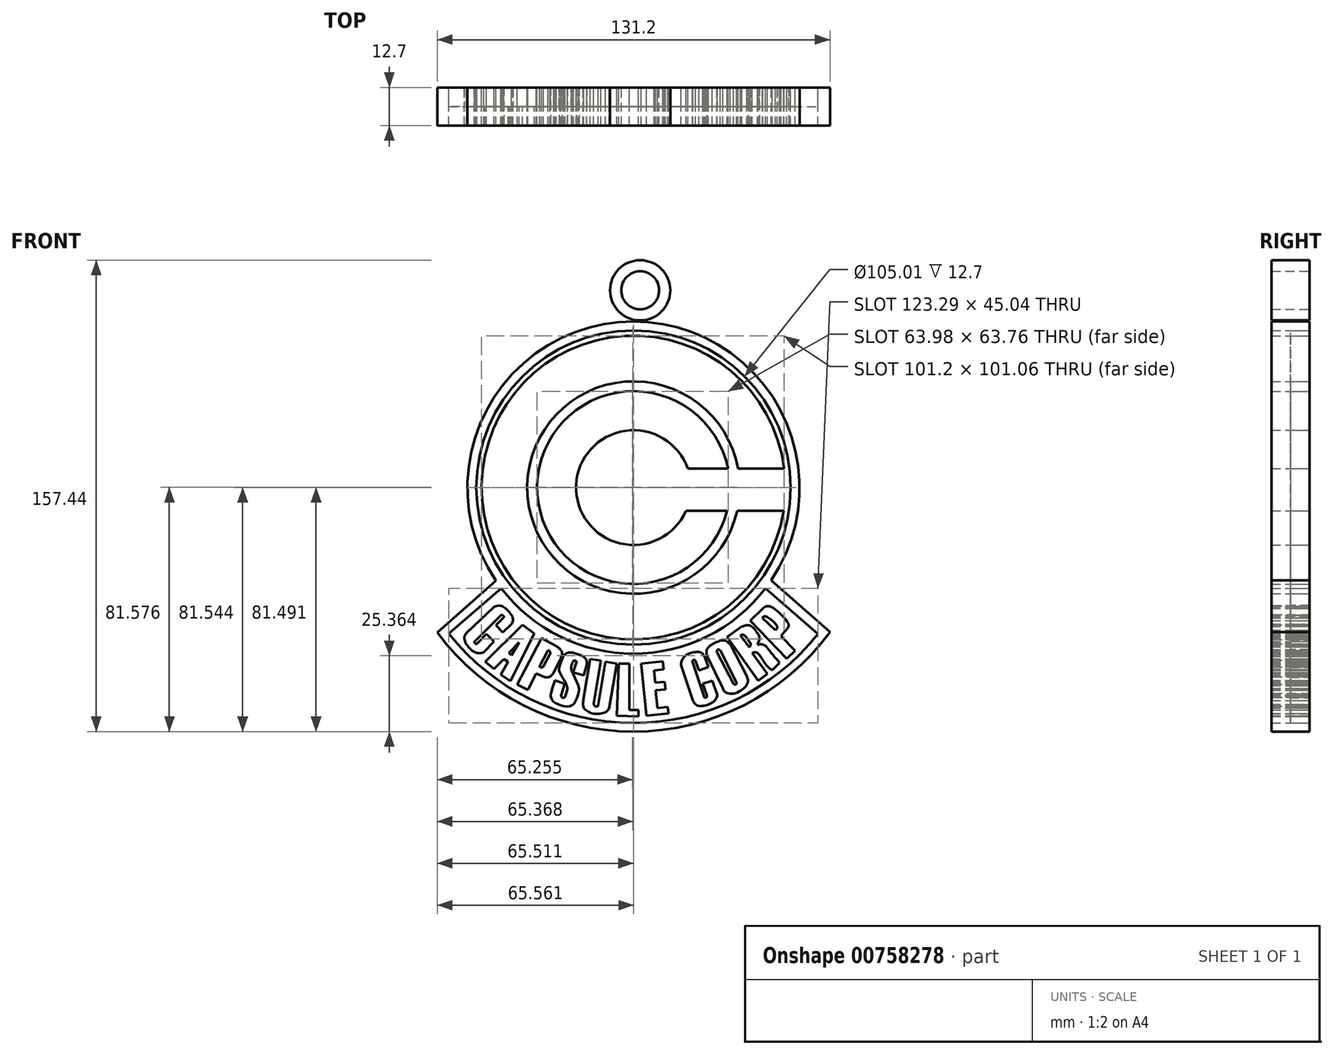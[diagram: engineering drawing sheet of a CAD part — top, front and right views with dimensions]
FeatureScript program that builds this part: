
annotation { "Feature Type Name" : "Feature", "Feature Type Description" : "" }
export const myFeature = defineFeature(function(context is Context, id is Id, definition is map)
    precondition{}
    {
        {
            var Q0;
            Q0=qCreatedBy(makeId("Front.planeOp"),FACE);
            var sketch = newSketch(context, id + "F0", { "sketchPlane" : qUnion([Q0])});
            skArc(sketch, "E0", {"start": v(-49.17, -26.74) * mm, "mid": v(40, 39.26) * mm, "end": v(-50.94, -24.27) * mm});
            skCircle(sketch, "E1", {"center": v(-5.04, 6.87) * mm, "radius": 52.5 * mm});
            skArc(sketch, "E2", {"start": v(45.3, 13.17) * mm, "mid": v(-55.76, 7.63) * mm, "end": v(45.09, -0.93) * mm});
            skArc(sketch, "E3", {"start": v(29.9, 13.17) * mm, "mid": v(-40.52, 7.64) * mm, "end": v(29.59, -0.93) * mm});
            skLineSegment(sketch, "E4", {"start": v(13.07, 13.17) * mm, "end": v(26.54, 13.17) * mm});
            skArc(sketch, "E5", {"start": v(26.54, 13.17) * mm, "mid": v(-37.23, 7.64) * mm, "end": v(26.2, -0.93) * mm});
            skArc(sketch, "E6", {"start": v(13.07, 13.17) * mm, "mid": v(-24.2, 7.68) * mm, "end": v(12.48, -0.93) * mm});
            skLineSegment(sketch, "E7", {"start": v(12.48, -0.93) * mm, "end": v(26.2, -0.93) * mm});
            skLineSegment(sketch, "E8.trimOffspring", {"start": v(29.9, 13.17) * mm, "end": v(45.3, 13.17) * mm});
            skLineSegment(sketch, "E9.trimOffspring", {"start": v(29.59, -0.93) * mm, "end": v(45.09, -0.93) * mm});
            skArc(sketch, "E10", {"start": v(-70.6, -41.54) * mm, "mid": v(-4.97, -74.62) * mm, "end": v(60.6, -41.43) * mm});
            skArc(sketch, "E11", {"start": v(-66.73, -41.9) * mm, "mid": v(-5.12, -71.78) * mm, "end": v(56.56, -42.03) * mm});
            skLineSegment(sketch, "E12", {"start": v(-49.17, -26.74) * mm, "end": v(-66.73, -41.9) * mm});
            skLineSegment(sketch, "E13", {"start": v(39.09, -26.74) * mm, "end": v(56.56, -42.03) * mm});
            skPoint(sketch, "E14.orphan", {"position": v(63.37, -48) * mm});
            skPoint(sketch, "E15.orphan", {"position": v(68.63, -48) * mm});
            skFitSpline(sketch, "E16", {"points": [v(-45.73, -38.7) * mm, v(-45.34, -37.46) * mm, v(-45.5, -36.25) * mm, v(-46.52, -34.75) * mm, v(-48.03, -33.33) * mm, v(-49.13, -32.7) * mm, v(-50.59, -32.6) * mm, v(-51.67, -33) * mm, v(-51.67, -33.09) * mm], "startDerivative": vector(4.88, 9.06) * mm, "endDerivative": vector(1, -2.13) * mm});
            skLineSegment(sketch, "E17", {"start": v(-45.73, -38.7) * mm, "end": v(-48.66, -41.56) * mm});
            skLineSegment(sketch, "E18", {"start": v(-48.66, -41.56) * mm, "end": v(-51.02, -39.14) * mm});
            skLineSegment(sketch, "E19", {"start": v(-51.02, -39.14) * mm, "end": v(-48.42, -36.6) * mm});
            skLineSegment(sketch, "E20", {"start": v(-51.67, -33) * mm, "end": v(-60.72, -41.6) * mm});
            skLineSegment(sketch, "E21", {"start": v(-50.94, -24.27) * mm, "end": v(-70.6, -41.54) * mm});
            skLineSegment(sketch, "E22", {"start": v(40.99, -24.1) * mm, "end": v(60.6, -41.43) * mm});
            skFitSpline(sketch, "E23", {"points": [v(-60.72, -41.6) * mm, v(-61.37, -42.57) * mm, v(-61.45, -44.07) * mm, v(-60.72, -45.65) * mm, v(-59.8, -46.78) * mm, v(-58.43, -47.9) * mm, v(-56.31, -48.46) * mm, v(-55.06, -48.06) * mm], "startDerivative": vector(-6.27, -7.14) * mm, "endDerivative": vector(10.78, 4.7) * mm});
            skLineSegment(sketch, "E24", {"start": v(-54.14, -42.08) * mm, "end": v(-51.68, -44.59) * mm});
            skLineSegment(sketch, "E25", {"start": v(-51.68, -44.59) * mm, "end": v(-55.06, -48.06) * mm});
            skLineSegment(sketch, "E26", {"start": v(-54.14, -42.08) * mm, "end": v(-57.31, -45.34) * mm});
            skFitSpline(sketch, "E27", {"points": [v(-57.31, -45.34) * mm, v(-58.13, -44.53) * mm], "startDerivative": vector(-1.08, -0.76) * mm, "endDerivative": vector(0.79, 1.04) * mm});
            skLineSegment(sketch, "E28", {"start": v(-58.13, -44.53) * mm, "end": v(-49.3, -35.84) * mm});
            skFitSpline(sketch, "E29", {"points": [v(-48.42, -36.6) * mm, v(-49.3, -35.84) * mm], "startDerivative": vector(1.01, 2.3) * mm, "endDerivative": vector(-0.38, -0.97) * mm});
            skLineSegment(sketch, "E30", {"start": v(-54.58, -51.2) * mm, "end": v(-42.15, -39.02) * mm});
            skLineSegment(sketch, "E31", {"start": v(-38.38, -41.89) * mm, "end": v(-46.08, -57.97) * mm});
            skLineSegment(sketch, "E32", {"start": v(-46.08, -57.97) * mm, "end": v(-49.2, -55.56) * mm});
            skLineSegment(sketch, "E33", {"start": v(-47.04, -51.35) * mm, "end": v(-49.2, -55.56) * mm});
            skLineSegment(sketch, "E34", {"start": v(-47.04, -51.35) * mm, "end": v(-48.37, -50.32) * mm});
            skLineSegment(sketch, "E35", {"start": v(-48.37, -50.32) * mm, "end": v(-51.65, -53.72) * mm});
            skLineSegment(sketch, "E36", {"start": v(-51.65, -53.72) * mm, "end": v(-54.58, -51.35) * mm});
            skLineSegment(sketch, "E37", {"start": v(-46.67, -48.42) * mm, "end": v(-45.84, -49.09) * mm});
            skLineSegment(sketch, "E38", {"start": v(-45.84, -49.09) * mm, "end": v(-43.26, -44.78) * mm});
            skLineSegment(sketch, "E39", {"start": v(-43.26, -44.78) * mm, "end": v(-46.67, -48.42) * mm});
            skLineSegment(sketch, "E40", {"start": v(-43.87, -58.92) * mm, "end": v(-35.8, -43.43) * mm});
            skLineSegment(sketch, "E41", {"start": v(-35.8, -43.43) * mm, "end": v(-30.79, -46.04) * mm});
            skFitSpline(sketch, "E42", {"points": [v(-30.79, -46.04) * mm, v(-29.73, -46.94) * mm, v(-28.9, -48.38) * mm, v(-29.6, -50.64) * mm], "startDerivative": vector(3.61, -2.78) * mm, "endDerivative": vector(-2.97, -6.2) * mm});
            skLineSegment(sketch, "E43", {"start": v(-29.6, -50.64) * mm, "end": v(-31.65, -54.83) * mm});
            skFitSpline(sketch, "E44", {"points": [v(-31.65, -54.83) * mm, v(-32.98, -56.33) * mm, v(-35.02, -56.33) * mm, v(-37.5, -55.23) * mm], "startDerivative": vector(-3.55, -5.73) * mm, "endDerivative": vector(-6.2, 2.71) * mm});
            skLineSegment(sketch, "E45", {"start": v(-37.5, -55.23) * mm, "end": v(-40.4, -60.63) * mm});
            skLineSegment(sketch, "E46", {"start": v(-40.4, -60.63) * mm, "end": v(-43.87, -58.92) * mm});
            skLineSegment(sketch, "E47", {"start": v(-33.6, -47.44) * mm, "end": v(-36.39, -52.85) * mm});
            skFitSpline(sketch, "E48", {"points": [v(-33.6, -47.44) * mm, v(-32.92, -48.73) * mm], "startDerivative": vector(1.37, 0.33) * mm, "endDerivative": vector(-1.26, -0.57) * mm});
            skFitSpline(sketch, "E49", {"points": [v(-36.39, -52.85) * mm, v(-35.08, -52.85) * mm], "startDerivative": vector(0.5, -1.16) * mm, "endDerivative": vector(0.36, 1.21) * mm});
            skLineSegment(sketch, "E50", {"start": v(-32.92, -48.73) * mm, "end": v(-35.08, -52.85) * mm});
            skFitSpline(sketch, "E51", {"points": [v(-20.61, -52.32) * mm, v(-20.81, -50.68) * mm, v(-22.1, -49.38) * mm, v(-24.35, -48.54) * mm, v(-25.54, -48.29) * mm, v(-27.44, -48.49) * mm, v(-28.48, -49.48) * mm], "startDerivative": vector(0.1, 10.55) * mm, "endDerivative": vector(-5.63, -7.7) * mm});
            skLineSegment(sketch, "E52", {"start": v(-20.61, -52.32) * mm, "end": v(-21.7, -55.9) * mm});
            skLineSegment(sketch, "E53", {"start": v(-21.7, -55.9) * mm, "end": v(-25.17, -54.85) * mm});
            skLineSegment(sketch, "E54", {"start": v(-25.17, -54.85) * mm, "end": v(-24.11, -51.38) * mm});
            skFitSpline(sketch, "E55", {"points": [v(-24.11, -51.38) * mm, v(-25.12, -51.02) * mm], "startDerivative": vector(0.7, 0.84) * mm, "endDerivative": vector(-0.65, -0.93) * mm});
            skFitSpline(sketch, "E56", {"points": [v(-25.12, -51.02) * mm, v(-25.47, -51.75) * mm, v(-25.81, -52.95) * mm, v(-25.75, -54.24) * mm], "startDerivative": vector(-1.2, -2.36) * mm, "endDerivative": vector(1.41, -4.25) * mm});
            skLineSegment(sketch, "E57", {"start": v(-25.75, -54.24) * mm, "end": v(-23.4, -59.28) * mm});
            skFitSpline(sketch, "E58", {"points": [v(-23.4, -59.28) * mm, v(-23.24, -60.16) * mm, v(-23.4, -61.5) * mm, v(-24.37, -64.45) * mm, v(-25.38, -65.64) * mm, v(-27.41, -66.29) * mm, v(-29.63, -65.74) * mm, v(-31.66, -64.81) * mm, v(-32.58, -63.38) * mm, v(-32.74, -62.6) * mm, v(-32.31, -60.7) * mm, v(-31.32, -57.57) * mm], "startDerivative": vector(3.29, -13.72) * mm, "endDerivative": vector(8.78, 26.62) * mm});
            skLineSegment(sketch, "E59", {"start": v(-31.32, -57.57) * mm, "end": v(-27.97, -58.6) * mm});
            skLineSegment(sketch, "E60", {"start": v(-27.97, -58.6) * mm, "end": v(-29.23, -62.7) * mm});
            skFitSpline(sketch, "E61", {"points": [v(-29.23, -62.7) * mm, v(-29, -63.17) * mm, v(-28.3, -63.35) * mm, v(-27.88, -62.98) * mm], "startDerivative": vector(0.4, -1.68) * mm, "endDerivative": vector(1.08, 1.5) * mm});
            skLineSegment(sketch, "E62", {"start": v(-27.88, -62.98) * mm, "end": v(-27.14, -60.5) * mm});
            skPoint(sketch, "E63.5.internal.snap0", {"position": v(-29.65, -58.08) * mm});
            skFitSpline(sketch, "E63", {"points": [v(-27.14, -60.5) * mm, v(-27.14, -60) * mm, v(-27.35, -59.18) * mm, v(-27.97, -57.84) * mm, v(-28.54, -56.84) * mm, v(-29.65, -54.92) * mm, v(-29.85, -53.23) * mm, v(-28.48, -49.48) * mm], "startDerivative": vector(0.32, 5.9) * mm, "endDerivative": vector(7.83, 18.03) * mm});
            skLineSegment(sketch, "E64", {"start": v(-19.52, -50.4) * mm, "end": v(-15.9, -50.86) * mm});
            skLineSegment(sketch, "E65", {"start": v(-15.9, -50.86) * mm, "end": v(-18.33, -65.47) * mm});
            skLineSegment(sketch, "E66", {"start": v(-19.52, -50.4) * mm, "end": v(-21.79, -63.88) * mm});
            skLineSegment(sketch, "E67", {"start": v(-14.4, -51.26) * mm, "end": v(-10.66, -51.89) * mm});
            skLineSegment(sketch, "E68", {"start": v(-10.66, -51.89) * mm, "end": v(-13.13, -66.7) * mm});
            skLineSegment(sketch, "E69", {"start": v(-14.4, -51.26) * mm, "end": v(-16.82, -65.8) * mm});
            skFitSpline(sketch, "E70", {"points": [v(-18.33, -65.47) * mm, v(-17.8, -66.17) * mm, v(-17.03, -66.14) * mm, v(-16.82, -65.8) * mm], "startDerivative": vector(1.06, -2.27) * mm, "endDerivative": vector(0.48, 1.48) * mm});
            skFitSpline(sketch, "E71", {"points": [v(-21.79, -63.88) * mm, v(-21.79, -66.4) * mm, v(-21.15, -67.27) * mm, v(-19.72, -68.22) * mm, v(-16.82, -68.75) * mm, v(-14.77, -68.29) * mm, v(-13.13, -66.7) * mm], "startDerivative": vector(-1.4, -8.83) * mm, "endDerivative": vector(3.28, 15.38) * mm});
            skLineSegment(sketch, "E72", {"start": v(-10.03, -51.89) * mm, "end": v(-10.66, -69.37) * mm});
            skLineSegment(sketch, "E73", {"start": v(-10.66, -69.37) * mm, "end": v(-3.4, -69.63) * mm});
            skLineSegment(sketch, "E74", {"start": v(-3.4, -69.63) * mm, "end": v(-3.4, -67.48) * mm});
            skLineSegment(sketch, "E75", {"start": v(-3.4, -67.48) * mm, "end": v(-6.45, -67.48) * mm});
            skLineSegment(sketch, "E76", {"start": v(-6.45, -67.48) * mm, "end": v(-6.45, -51.89) * mm});
            skLineSegment(sketch, "E77", {"start": v(-6.45, -51.89) * mm, "end": v(-10.03, -51.89) * mm});
            skLineSegment(sketch, "E78", {"start": v(-2.53, -51.89) * mm, "end": v(-0.76, -69.37) * mm});
            skLineSegment(sketch, "E79", {"start": v(-0.76, -69.37) * mm, "end": v(6.66, -68.61) * mm});
            skLineSegment(sketch, "E80", {"start": v(6.66, -68.61) * mm, "end": v(6.44, -66.42) * mm});
            skLineSegment(sketch, "E81", {"start": v(6.44, -66.42) * mm, "end": v(2.96, -66.77) * mm});
            skLineSegment(sketch, "E82", {"start": v(2.96, -66.77) * mm, "end": v(2.35, -60.83) * mm});
            skLineSegment(sketch, "E83", {"start": v(2.35, -60.83) * mm, "end": v(5.6, -60.5) * mm});
            skLineSegment(sketch, "E84", {"start": v(5.6, -60.5) * mm, "end": v(5.36, -58.02) * mm});
            skLineSegment(sketch, "E85", {"start": v(5.36, -58.02) * mm, "end": v(2.25, -58.34) * mm});
            skLineSegment(sketch, "E86", {"start": v(2.25, -58.34) * mm, "end": v(1.83, -54.15) * mm});
            skLineSegment(sketch, "E87", {"start": v(1.83, -54.15) * mm, "end": v(4.96, -53.83) * mm});
            skLineSegment(sketch, "E88", {"start": v(4.96, -53.83) * mm, "end": v(4.7, -51.17) * mm});
            skLineSegment(sketch, "E89", {"start": v(4.7, -51.17) * mm, "end": v(-2.53, -51.89) * mm});
            skLineSegment(sketch, "E90", {"start": v(10.8, -52.42) * mm, "end": v(14.8, -64.3) * mm});
            skLineSegment(sketch, "E91", {"start": v(19, -50.23) * mm, "end": v(20.03, -53.08) * mm});
            skLineSegment(sketch, "E92", {"start": v(20.03, -53.08) * mm, "end": v(16.83, -54.24) * mm});
            skLineSegment(sketch, "E93", {"start": v(16.83, -54.24) * mm, "end": v(15.66, -51) * mm});
            skLineSegment(sketch, "E94", {"start": v(14.65, -51.24) * mm, "end": v(18.4, -62.74) * mm});
            skLineSegment(sketch, "E95", {"start": v(21.31, -57.59) * mm, "end": v(22.87, -62.24) * mm});
            skLineSegment(sketch, "E96", {"start": v(21.31, -57.59) * mm, "end": v(18.13, -58.66) * mm});
            skLineSegment(sketch, "E97", {"start": v(18.13, -58.66) * mm, "end": v(19.46, -62.62) * mm});
            skFitSpline(sketch, "E98", {"points": [v(19, -50.23) * mm, v(17.74, -48.36) * mm, v(15.6, -48.06) * mm, v(13.24, -48.73) * mm, v(11.44, -50.23) * mm, v(10.8, -52.42) * mm], "startDerivative": vector(-4.84, 8.42) * mm, "endDerivative": vector(-1.62, -14.3) * mm});
            skFitSpline(sketch, "E99", {"points": [v(14.8, -64.3) * mm, v(15.97, -65.77) * mm, v(19, -65.92) * mm, v(21.58, -64.74) * mm, v(22.44, -63.83) * mm, v(22.87, -62.24) * mm], "startDerivative": vector(4.67, -9.06) * mm, "endDerivative": vector(-1.2, 11.4) * mm});
            skFitSpline(sketch, "E100", {"points": [v(14.65, -51.24) * mm, v(14.8, -50.86) * mm, v(15.66, -51) * mm], "startDerivative": vector(0.62, 1.12) * mm, "endDerivative": vector(1.2, -2.47) * mm});
            skFitSpline(sketch, "E101", {"points": [v(18.4, -62.74) * mm, v(18.66, -63.2) * mm, v(19.46, -63.07) * mm, v(19.46, -62.62) * mm], "startDerivative": vector(0.35, -1.81) * mm, "endDerivative": vector(-0.55, 1.7) * mm});
            skFitSpline(sketch, "E102", {"points": [v(19.46, -49.28) * mm, v(19.46, -47.3) * mm, v(21.22, -45.5) * mm, v(23.21, -44.53) * mm, v(25.2, -44.15) * mm, v(27.2, -45.37) * mm], "startDerivative": vector(-2, 10.78) * mm, "endDerivative": vector(9.45, -8) * mm});
            skFitSpline(sketch, "E103", {"points": [v(22.86, -48.22) * mm, v(22.9, -47.49) * mm, v(23.34, -47.23) * mm, v(23.92, -47.49) * mm], "startDerivative": vector(-0.3, 2.28) * mm, "endDerivative": vector(1.7, -1.14) * mm});
            skFitSpline(sketch, "E104", {"points": [v(28.42, -58.72) * mm, v(28.97, -58.94) * mm, v(29.33, -58.68) * mm, v(29.44, -58.13) * mm], "startDerivative": vector(1.6, -0.99) * mm, "endDerivative": vector(0.1, 1.72) * mm});
            skFitSpline(sketch, "E105", {"points": [v(32.78, -56.1) * mm, v(33.17, -57.58) * mm, v(32.56, -59.38) * mm, v(30.8, -60.9) * mm, v(27.92, -62) * mm, v(25.43, -61.26) * mm, v(24.77, -60.2) * mm], "startDerivative": vector(4.08, -9.97) * mm, "endDerivative": vector(-3.36, 8.57) * mm});
            skLineSegment(sketch, "E106", {"start": v(19.46, -49.28) * mm, "end": v(24.77, -60.2) * mm});
            skLineSegment(sketch, "E107", {"start": v(22.86, -48.22) * mm, "end": v(28.42, -58.72) * mm});
            skLineSegment(sketch, "E108", {"start": v(23.92, -47.49) * mm, "end": v(29.43, -58.33) * mm});
            skLineSegment(sketch, "E109", {"start": v(27.2, -45.37) * mm, "end": v(32.78, -56.1) * mm});
            skLineSegment(sketch, "E110", {"start": v(26.21, -43.06) * mm, "end": v(36.6, -57.58) * mm});
            skLineSegment(sketch, "E111", {"start": v(36.6, -57.58) * mm, "end": v(39.66, -55.4) * mm});
            skLineSegment(sketch, "E112", {"start": v(39.66, -55.4) * mm, "end": v(34.63, -48.36) * mm});
            skLineSegment(sketch, "E113", {"start": v(30.64, -42.51) * mm, "end": v(33.53, -46.4) * mm});
            skLineSegment(sketch, "E114", {"start": v(26.21, -43.06) * mm, "end": v(31.13, -39.54) * mm});
            skLineSegment(sketch, "E115", {"start": v(33.97, -37.6) * mm, "end": v(46.13, -50.3) * mm});
            skLineSegment(sketch, "E116", {"start": v(46.13, -50.3) * mm, "end": v(48.94, -47.6) * mm});
            skLineSegment(sketch, "E117", {"start": v(48.94, -47.6) * mm, "end": v(44.3, -42.76) * mm});
            skLineSegment(sketch, "E118", {"start": v(33.97, -37.6) * mm, "end": v(38.2, -33.54) * mm});
            skLineSegment(sketch, "E119", {"start": v(38.05, -36.64) * mm, "end": v(42.38, -40.7) * mm});
            skFitSpline(sketch, "E120", {"points": [v(30.64, -42.51) * mm, v(31.14, -42.28) * mm, v(31.78, -42.32) * mm, v(33.9, -44.94) * mm, v(34.06, -45.98) * mm, v(33.53, -46.4) * mm], "startDerivative": vector(3.47, 1.82) * mm, "endDerivative": vector(-4.1, -2.24) * mm});
            skFitSpline(sketch, "E121", {"points": [v(31.13, -39.54) * mm, v(32.64, -39.16) * mm, v(34.54, -39.54) * mm, v(36.48, -41.95) * mm, v(37.05, -43.49) * mm, v(36.32, -45.63) * mm], "startDerivative": vector(8.34, 2.68) * mm, "endDerivative": vector(-5.1, -10.9) * mm});
            skFitSpline(sketch, "E122", {"points": [v(36.32, -45.63) * mm, v(38.42, -45.63) * mm, v(40.55, -47.82) * mm, v(43.79, -51.66) * mm], "startDerivative": vector(8.26, 1.5) * mm, "endDerivative": vector(8.33, -9.53) * mm});
            skFitSpline(sketch, "E123", {"points": [v(34.63, -48.36) * mm, v(36.32, -48.36) * mm, v(39.23, -52.37) * mm, v(41.36, -54.1) * mm], "startDerivative": vector(6.71, 2.12) * mm, "endDerivative": vector(6.63, -3.78) * mm});
            skLineSegment(sketch, "E124", {"start": v(41.36, -54.1) * mm, "end": v(43.79, -51.66) * mm});
            skFitSpline(sketch, "E125", {"points": [v(38.2, -33.54) * mm, v(41.91, -33.54) * mm, v(46.72, -38.8) * mm, v(44.3, -42.76) * mm], "startDerivative": vector(13.84, 13.65) * mm, "endDerivative": vector(-15.96, -22.94) * mm});
            skFitSpline(sketch, "E126", {"points": [v(38.05, -36.64) * mm, v(38.99, -36.12) * mm, v(42.94, -39.58) * mm, v(42.38, -40.7) * mm], "startDerivative": vector(2.8, 3.95) * mm, "endDerivative": vector(-4.3, -3.47) * mm});
            skLineSegment(sketch, "E127", {"start": v(-42.15, -39.02) * mm, "end": v(-38.38, -41.89) * mm});
            skSolve(sketch);
        }
        {
            var Q0;
            Q0=makeQuery(id+"F0.imprint","IMPRINT",FACE,{"disambiguationData":[TD([[makeQuery(id+"F0.imprint","IMPRINT",EDGE,{"derivedFrom":sQuery(id+"F0.wireOp",EDGE,"E1")}),-1.0]])]});
            extrude(context, id + "F1", {"entities" : qUnion([Q0]), "depth" : 12.7 * mm, "offsetDistance" : 25.4 * mm});
        }
        {
            var Q0;
            Q0=makeQuery(id+"F0.imprint","IMPRINT",FACE,{"disambiguationData":[TD([[makeQuery(id+"F0.imprint","IMPRINT",EDGE,{"derivedFrom":sQuery(id+"F0.wireOp",EDGE,"E2")}),1.0]])]});
            extrude(context, id + "F2", {"entities" : qUnion([Q0]), "depth" : 12.7 * mm, "offsetDistance" : 25.4 * mm});
        }
        {
            var Q0;
            Q0=makeQuery(id+"F0.imprint","IMPRINT",FACE,{"disambiguationData":[TD([[makeQuery(id+"F0.imprint","IMPRINT",EDGE,{"derivedFrom":sQuery(id+"F0.wireOp",EDGE,"E4")}),1.0]])]});
            var Q1;
            {var subQ1=sQuery(id+"F0.wireOp",EDGE,"E17");Q1=makeQuery(id+"F0.imprint","IMPRINT",FACE,{"disambiguationData":[TD([[makeQuery(id+"F0.imprint","IMPRINT",EDGE,{"derivedFrom":subQ1}),-1.0]])]});}
            extrude(context, id + "F3", {"entities" : qUnion([Q0, Q1]), "depth" : 12.7 * mm, "offsetDistance" : 25.4 * mm});
        }
        {
            var Q0;
            Q0=makeQuery(id+"F0.imprint","IMPRINT",FACE,{"disambiguationData":[TD([[makeQuery(id+"F0.imprint","IMPRINT",EDGE,{"derivedFrom":sQuery(id+"F0.wireOp",EDGE,"E40")}),-1.0]])]});
            extrude(context, id + "F4", {"entities" : qUnion([Q0]), "depth" : 12.7 * mm, "offsetDistance" : 25.4 * mm});
        }
        {
            var Q0;
            Q0=makeQuery(id+"F0.imprint","IMPRINT",FACE,{"disambiguationData":[TD([[makeQuery(id+"F0.imprint","IMPRINT",EDGE,{"derivedFrom":sQuery(id+"F0.wireOp",EDGE,"E51")}),1.0]])]});
            extrude(context, id + "F5", {"entities" : qUnion([Q0]), "depth" : 12.7 * mm, "offsetDistance" : 25.4 * mm});
        }
        {
            var Q0;
            Q0=makeQuery(id+"F0.imprint","IMPRINT",FACE,{"disambiguationData":[TD([[makeQuery(id+"F0.imprint","IMPRINT",EDGE,{"derivedFrom":sQuery(id+"F0.wireOp",EDGE,"E64")}),-1.0]])]});
            extrude(context, id + "F6", {"entities" : qUnion([Q0]), "depth" : 12.7 * mm, "offsetDistance" : 25.4 * mm});
        }
        {
            var Q0;
            Q0=makeQuery(id+"F0.imprint","IMPRINT",FACE,{"disambiguationData":[TD([[makeQuery(id+"F0.imprint","IMPRINT",EDGE,{"derivedFrom":sQuery(id+"F0.wireOp",EDGE,"E72")}),1.0]])]});
            extrude(context, id + "F7", {"entities" : qUnion([Q0]), "depth" : 12.7 * mm, "offsetDistance" : 25.4 * mm});
        }
        {
            var Q0;
            Q0=makeQuery(id+"F0.imprint","IMPRINT",FACE,{"disambiguationData":[TD([[makeQuery(id+"F0.imprint","IMPRINT",EDGE,{"derivedFrom":sQuery(id+"F0.wireOp",EDGE,"E78")}),1.0]])]});
            extrude(context, id + "F8", {"entities" : qUnion([Q0]), "depth" : 12.7 * mm, "offsetDistance" : 25.4 * mm});
        }
        {
            var Q0;
            Q0=makeQuery(id+"F0.imprint","IMPRINT",FACE,{"disambiguationData":[TD([[makeQuery(id+"F0.imprint","IMPRINT",EDGE,{"derivedFrom":sQuery(id+"F0.wireOp",EDGE,"E90")}),1.0]])]});
            extrude(context, id + "F9", {"entities" : qUnion([Q0]), "depth" : 12.7 * mm, "offsetDistance" : 25.4 * mm});
        }
        {
            var Q0;
            Q0=makeQuery(id+"F0.imprint","IMPRINT",FACE,{"disambiguationData":[TD([[makeQuery(id+"F0.imprint","IMPRINT",EDGE,{"derivedFrom":sQuery(id+"F0.wireOp",EDGE,"E102")}),-1.0]])]});
            extrude(context, id + "F10", {"entities" : qUnion([Q0]), "depth" : 12.7 * mm, "offsetDistance" : 25.4 * mm});
        }
        {
            var Q0;
            Q0=makeQuery(id+"F0.imprint","IMPRINT",FACE,{"disambiguationData":[TD([[makeQuery(id+"F0.imprint","IMPRINT",EDGE,{"derivedFrom":sQuery(id+"F0.wireOp",EDGE,"E110")}),1.0]])]});
            extrude(context, id + "F11", {"entities" : qUnion([Q0]), "depth" : 12.7 * mm, "offsetDistance" : 25.4 * mm});
        }
        {
            var Q0;
            Q0=makeQuery(id+"F0.imprint","IMPRINT",FACE,{"disambiguationData":[TD([[makeQuery(id+"F0.imprint","IMPRINT",EDGE,{"derivedFrom":sQuery(id+"F0.wireOp",EDGE,"E115")}),1.0]])]});
            extrude(context, id + "F12", {"entities" : qUnion([Q0]), "depth" : 12.7 * mm, "offsetDistance" : 25.4 * mm});
        }
        {
            var Q0;
            Q0=makeQuery(id+"F0.imprint","IMPRINT",FACE,{"disambiguationData":[TD([[makeQuery(id+"F0.imprint","IMPRINT",EDGE,{"derivedFrom":sQuery(id+"F0.wireOp",EDGE,"E1")}),1.0]])]});
            extrude(context, id + "F13", {"entities" : qUnion([Q0]), "depth" : 6.35 * mm, "offsetDistance" : 25.4 * mm});
        }
        {
            var Q0;
            Q0=makeQuery(id+"F0.imprint","IMPRINT",FACE,{"disambiguationData":[TD([[makeQuery(id+"F0.imprint","IMPRINT",EDGE,{"derivedFrom":sQuery(id+"F0.wireOp",EDGE,"E11")}),1.0]])]});
            extrude(context, id + "F14", {"entities" : qUnion([Q0]), "depth" : 6.35 * mm, "offsetDistance" : 25.4 * mm});
        }
        {
            var Q0;
            Q0=makeQuery(id+"F0.imprint","IMPRINT",FACE,{"disambiguationData":[TD([[makeQuery(id+"F0.imprint","IMPRINT",EDGE,{"derivedFrom":sQuery(id+"F0.wireOp",EDGE,"E47")}),1.0]])]});
            var Q1;
            {var subQ0=sQuery(id+"F0.wireOp",EDGE,"E103");Q1=makeQuery(id+"F0.imprint","IMPRINT",FACE,{"disambiguationData":[TD([[makeQuery(id+"F0.imprint","IMPRINT",EDGE,{"derivedFrom":subQ0}),-1.0]])]});}
            var Q2;
            Q2=makeQuery(id+"F0.imprint","IMPRINT",FACE,{"disambiguationData":[TD([[makeQuery(id+"F0.imprint","IMPRINT",EDGE,{"derivedFrom":sQuery(id+"F0.wireOp",EDGE,"E113")}),1.0]])]});
            var Q3;
            Q3=makeQuery(id+"F0.imprint","IMPRINT",FACE,{"disambiguationData":[TD([[makeQuery(id+"F0.imprint","IMPRINT",EDGE,{"derivedFrom":sQuery(id+"F0.wireOp",EDGE,"E119")}),1.0]])]});
            var Q4;
            Q4=makeQuery(id+"F0.imprint","IMPRINT",FACE,{"disambiguationData":[TD([[makeQuery(id+"F0.imprint","IMPRINT",EDGE,{"derivedFrom":sQuery(id+"F0.wireOp",EDGE,"E37")}),1.0]])]});
            extrude(context, id + "F15", {"entities" : qUnion([Q0, Q1, Q2, Q3, Q4]), "depth" : 6.35 * mm, "offsetDistance" : 25.4 * mm});
        }
        {
            var Q0;
            Q0=makeQuery(id+"F14.opExtrude","CAP_FACE",FACE,{"disambiguationData":[OSD([sQuery(id+"F0.wireOp",EDGE,"E0"),sQuery(id+"F0.wireOp",EDGE,"E11"),sQuery(id+"F0.wireOp",EDGE,"E12"),sQuery(id+"F0.wireOp",EDGE,"E13"),sQuery(id+"F0.wireOp",EDGE,"E16"),sQuery(id+"F0.wireOp",EDGE,"E17"),sQuery(id+"F0.wireOp",EDGE,"E18"),sQuery(id+"F0.wireOp",EDGE,"E19"),sQuery(id+"F0.wireOp",EDGE,"E20"),sQuery(id+"F0.wireOp",EDGE,"E23"),sQuery(id+"F0.wireOp",EDGE,"E24"),sQuery(id+"F0.wireOp",EDGE,"E25"),sQuery(id+"F0.wireOp",EDGE,"E26"),sQuery(id+"F0.wireOp",EDGE,"E27"),sQuery(id+"F0.wireOp",EDGE,"E28"),sQuery(id+"F0.wireOp",EDGE,"E29"),sQuery(id+"F0.wireOp",EDGE,"E37"),sQuery(id+"F0.wireOp",EDGE,"E38"),sQuery(id+"F0.wireOp",EDGE,"E39"),sQuery(id+"F0.wireOp",EDGE,"E40"),sQuery(id+"F0.wireOp",EDGE,"E41"),sQuery(id+"F0.wireOp",EDGE,"E42"),sQuery(id+"F0.wireOp",EDGE,"E43"),sQuery(id+"F0.wireOp",EDGE,"E44"),sQuery(id+"F0.wireOp",EDGE,"E45"),sQuery(id+"F0.wireOp",EDGE,"E46"),sQuery(id+"F0.wireOp",EDGE,"E51"),sQuery(id+"F0.wireOp",EDGE,"E52"),sQuery(id+"F0.wireOp",EDGE,"E53"),sQuery(id+"F0.wireOp",EDGE,"E54"),sQuery(id+"F0.wireOp",EDGE,"E55"),sQuery(id+"F0.wireOp",EDGE,"E56"),sQuery(id+"F0.wireOp",EDGE,"E57"),sQuery(id+"F0.wireOp",EDGE,"E58"),sQuery(id+"F0.wireOp",EDGE,"E59"),sQuery(id+"F0.wireOp",EDGE,"E60"),sQuery(id+"F0.wireOp",EDGE,"E61"),sQuery(id+"F0.wireOp",EDGE,"E62"),sQuery(id+"F0.wireOp",EDGE,"E63"),sQuery(id+"F0.wireOp",EDGE,"E64"),sQuery(id+"F0.wireOp",EDGE,"E65"),sQuery(id+"F0.wireOp",EDGE,"E66"),sQuery(id+"F0.wireOp",EDGE,"E67"),sQuery(id+"F0.wireOp",EDGE,"E68"),sQuery(id+"F0.wireOp",EDGE,"E69"),sQuery(id+"F0.wireOp",EDGE,"E70"),sQuery(id+"F0.wireOp",EDGE,"E71"),sQuery(id+"F0.wireOp",EDGE,"E72"),sQuery(id+"F0.wireOp",EDGE,"E73"),sQuery(id+"F0.wireOp",EDGE,"E74"),sQuery(id+"F0.wireOp",EDGE,"E75"),sQuery(id+"F0.wireOp",EDGE,"E76"),sQuery(id+"F0.wireOp",EDGE,"E77"),sQuery(id+"F0.wireOp",EDGE,"E78"),sQuery(id+"F0.wireOp",EDGE,"E79"),sQuery(id+"F0.wireOp",EDGE,"E80"),sQuery(id+"F0.wireOp",EDGE,"E81"),sQuery(id+"F0.wireOp",EDGE,"E82"),sQuery(id+"F0.wireOp",EDGE,"E83"),sQuery(id+"F0.wireOp",EDGE,"E84"),sQuery(id+"F0.wireOp",EDGE,"E85"),sQuery(id+"F0.wireOp",EDGE,"E86"),sQuery(id+"F0.wireOp",EDGE,"E87"),sQuery(id+"F0.wireOp",EDGE,"E88"),sQuery(id+"F0.wireOp",EDGE,"E89"),sQuery(id+"F0.wireOp",EDGE,"E90"),sQuery(id+"F0.wireOp",EDGE,"E91"),sQuery(id+"F0.wireOp",EDGE,"E92"),sQuery(id+"F0.wireOp",EDGE,"E93"),sQuery(id+"F0.wireOp",EDGE,"E94"),sQuery(id+"F0.wireOp",EDGE,"E95"),sQuery(id+"F0.wireOp",EDGE,"E96"),sQuery(id+"F0.wireOp",EDGE,"E97"),sQuery(id+"F0.wireOp",EDGE,"E98"),sQuery(id+"F0.wireOp",EDGE,"E99"),sQuery(id+"F0.wireOp",EDGE,"E100"),sQuery(id+"F0.wireOp",EDGE,"E101"),sQuery(id+"F0.wireOp",EDGE,"E102"),sQuery(id+"F0.wireOp",EDGE,"E105"),sQuery(id+"F0.wireOp",EDGE,"E106"),sQuery(id+"F0.wireOp",EDGE,"E109"),sQuery(id+"F0.wireOp",EDGE,"E110"),sQuery(id+"F0.wireOp",EDGE,"E111"),sQuery(id+"F0.wireOp",EDGE,"E112"),sQuery(id+"F0.wireOp",EDGE,"E114"),sQuery(id+"F0.wireOp",EDGE,"E115"),sQuery(id+"F0.wireOp",EDGE,"E116"),sQuery(id+"F0.wireOp",EDGE,"E117"),sQuery(id+"F0.wireOp",EDGE,"E118"),sQuery(id+"F0.wireOp",EDGE,"E121"),sQuery(id+"F0.wireOp",EDGE,"E122"),sQuery(id+"F0.wireOp",EDGE,"E123"),sQuery(id+"F0.wireOp",EDGE,"E124"),sQuery(id+"F0.wireOp",EDGE,"E125")])],"isStart":false});
            var sketch = newSketch(context, id + "F16", { "sketchPlane" : qUnion([Q0])});
            skLineSegment(sketch, "E128", {"start": v(-42.17, -39) * mm, "end": v(-38.18, -41.84) * mm});
            skLineSegment(sketch, "E129", {"start": v(-38.18, -41.84) * mm, "end": v(-46.11, -57.83) * mm});
            skLineSegment(sketch, "E130", {"start": v(-46.11, -57.83) * mm, "end": v(-49.3, -55.62) * mm});
            skLineSegment(sketch, "E131", {"start": v(-49.3, -55.62) * mm, "end": v(-46.96, -51.3) * mm});
            skLineSegment(sketch, "E132", {"start": v(-42.17, -39) * mm, "end": v(-54.6, -51.34) * mm});
            skLineSegment(sketch, "E133", {"start": v(-54.6, -51.34) * mm, "end": v(-51.58, -53.67) * mm});
            skLineSegment(sketch, "E134", {"start": v(-51.58, -53.67) * mm, "end": v(-48.28, -50.36) * mm});
            skLineSegment(sketch, "E135", {"start": v(-48.28, -50.36) * mm, "end": v(-46.96, -51.3) * mm});
            skLineSegment(sketch, "E136", {"start": v(-46.67, -48.42) * mm, "end": v(-45.84, -49.09) * mm});
            skLineSegment(sketch, "E137", {"start": v(-45.84, -49.09) * mm, "end": v(-43.26, -44.78) * mm});
            skLineSegment(sketch, "E138", {"start": v(-43.26, -44.78) * mm, "end": v(-46.67, -48.42) * mm});
            skSolve(sketch);
        }
        {
            var Q0;
            Q0 = qSketchRegion(id + "F16", true);
            var Q1;
            Q1=makeQuery(id+"F16.imprint","IMPRINT",FACE,{"disambiguationData":[TD([[makeQuery(id+"F16.imprint","IMPRINT",EDGE,{"derivedFrom":sQuery(id+"F16.wireOp",EDGE,"E128")}),-1.0]])]});
            extrude(context, id + "F17", {"entities" : qUnion([Q0, Q1]), "operationType" : NewBodyOperationType.ADD, "depth" : 6.35 * mm, "offsetDistance" : 25.4 * mm});
        }
        {
            var Q0;
            Q0=qCreatedBy(makeId("Front.planeOp"),FACE);
            var sketch = newSketch(context, id + "F18", { "sketchPlane" : qUnion([Q0])});
            skCircle(sketch, "E139", {"center": v(-2.8, 72.77) * mm, "radius": 10.05 * mm});
            skCircle(sketch, "E140", {"center": v(-2.8, 72.77) * mm, "radius": 6.35 * mm});
            skSolve(sketch);
        }
        {
            var Q0;
            Q0=makeQuery(id+"F18.imprint","IMPRINT",FACE,{"disambiguationData":[TD([[makeQuery(id+"F18.imprint","IMPRINT",EDGE,{"derivedFrom":sQuery(id+"F18.wireOp",EDGE,"E139")}),1.0]])]});
            extrude(context, id + "F19", {"entities" : qUnion([Q0]), "depth" : 12.7 * mm, "offsetDistance" : 25.4 * mm});
        }
    });
